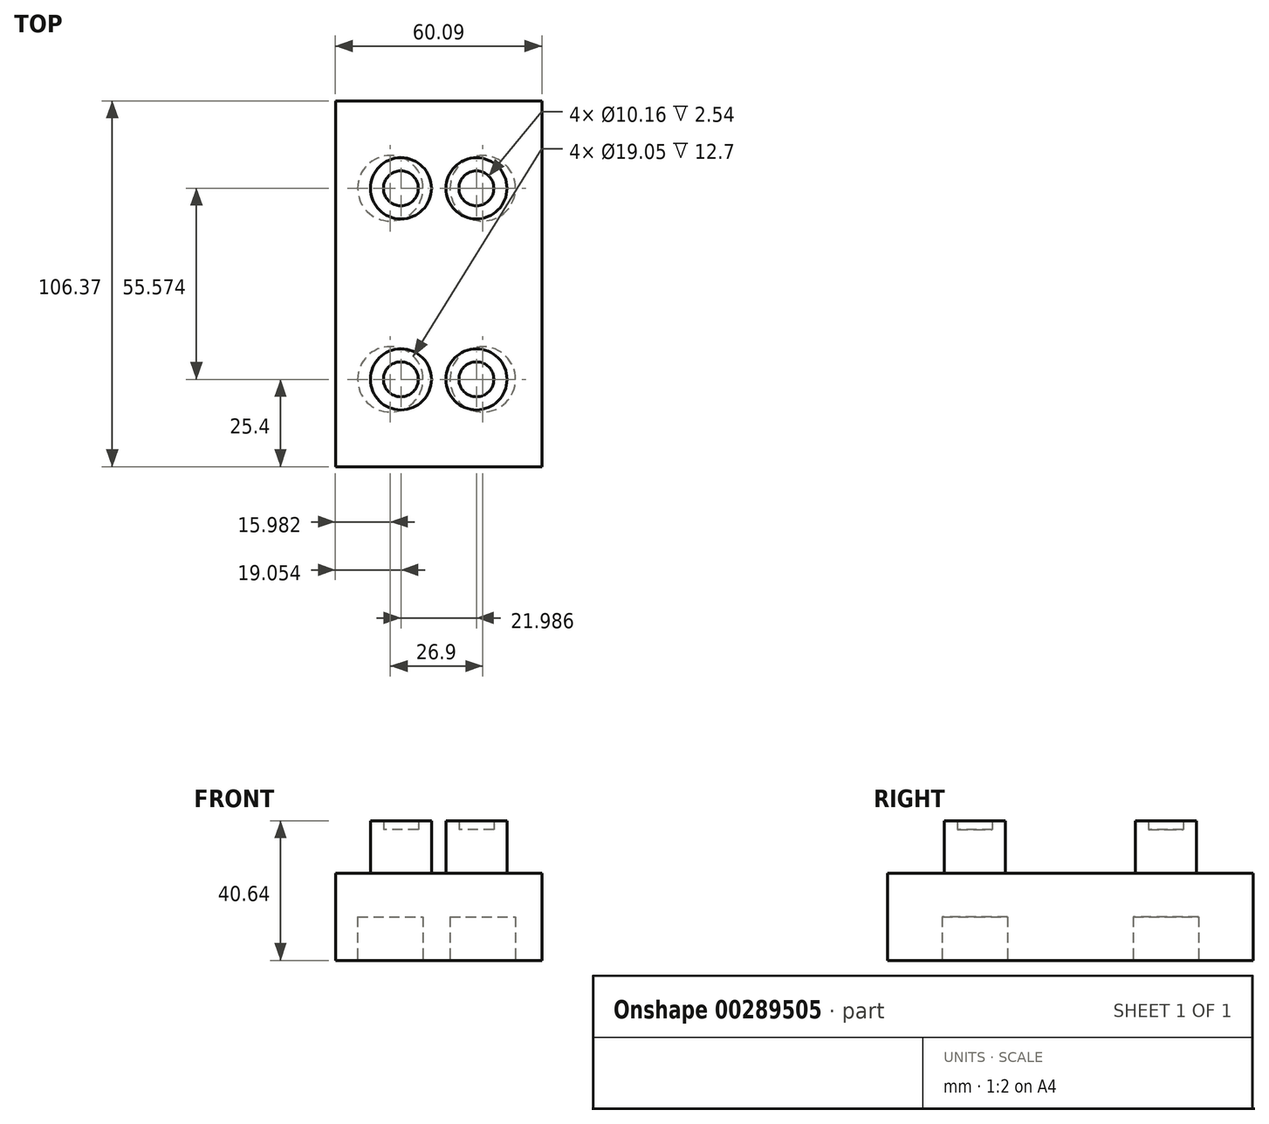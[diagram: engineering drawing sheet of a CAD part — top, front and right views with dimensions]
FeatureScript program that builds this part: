
annotation { "Feature Type Name" : "Feature", "Feature Type Description" : "" }
export const myFeature = defineFeature(function(context is Context, id is Id, definition is map)
    precondition{}
    {
        {
            var Q0;
            Q0=qCreatedBy(makeId("Top.planeOp"),FACE);
            var sketch = newSketch(context, id + "F0", { "sketchPlane" : qUnion([Q0])});
            skLineSegment(sketch, "E0.bottom", {"start": v(-60.09, -63.54) * mm, "end": v(0, -63.54) * mm});
            skLineSegment(sketch, "E0.top", {"start": v(-60.09, 42.83) * mm, "end": v(0, 42.83) * mm});
            skLineSegment(sketch, "E0.left", {"start": v(-60.09, -63.54) * mm, "end": v(-60.09, 42.83) * mm});
            skLineSegment(sketch, "E0.right", {"start": v(0, -63.54) * mm, "end": v(0, 42.83) * mm});
            skSolve(sketch);
        }
        {
            var Q0;
            Q0=makeQuery(id+"F0.imprint","IMPRINT",FACE,{"disambiguationData":[TD([[makeQuery(id+"F0.imprint","IMPRINT",EDGE,{"derivedFrom":sQuery(id+"F0.wireOp",EDGE,"E0.bottom")}),1.0]])]});
            extrude(context, id + "F1", {"entities" : qUnion([Q0]), "depth" : 25.4 * mm});
        }
        {
            var Q0;
            Q0=makeQuery(id+"F1.opExtrude","CAP_FACE",FACE,{"disambiguationData":[OSD([sQuery(id+"F0.wireOp",EDGE,"E0.bottom"),sQuery(id+"F0.wireOp",EDGE,"E0.top"),sQuery(id+"F0.wireOp",EDGE,"E0.left"),sQuery(id+"F0.wireOp",EDGE,"E0.right")])],"isStart":false});
            var sketch = newSketch(context, id + "F2", { "sketchPlane" : qUnion([Q0])});
            skLineSegment(sketch, "E1", {"start": v(-19.05, -63.54) * mm, "end": v(-19.05, -38.14) * mm});
            skLineSegment(sketch, "E2", {"start": v(-19.05, 42.83) * mm, "end": v(-19.05, 17.43) * mm});
            skLineSegment(sketch, "E3", {"start": v(0, 15.67) * mm, "end": v(-19.05, 15.67) * mm});
            skLineSegment(sketch, "E4", {"start": v(-60.09, 17.43) * mm, "end": v(-41.04, 17.43) * mm});
            skLineSegment(sketch, "E5", {"start": v(-41.04, 17.43) * mm, "end": v(-41.04, 42.83) * mm});
            skLineSegment(sketch, "E6", {"start": v(0, -38.14) * mm, "end": v(-19.05, -38.14) * mm});
            skLineSegment(sketch, "E7", {"start": v(-60.09, -38.14) * mm, "end": v(-41.04, -38.14) * mm});
            skLineSegment(sketch, "E8", {"start": v(-41.04, -38.14) * mm, "end": v(-41.04, -63.54) * mm});
            skCircle(sketch, "E9", {"center": v(-19.05, -38.14) * mm, "radius": 8.9 * mm});
            skCircle(sketch, "E10", {"center": v(-41.04, -38.14) * mm, "radius": 8.9 * mm});
            skCircle(sketch, "E11", {"center": v(-41.04, 17.43) * mm, "radius": 8.9 * mm});
            skCircle(sketch, "E12", {"center": v(-19.05, 17.43) * mm, "radius": 8.9 * mm});
            skSolve(sketch);
        }
        {
            var Q0;
            {var subQ0=sQuery(id+"F2.wireOp",EDGE,"E6");var subQ1=sQuery(id+"F2.wireOp",EDGE,"E1");var subQ2=makeQuery(id+"F2.imprint","INTERSECT",VERTEX,{"derivedFrom":[subQ1,subQ0]});Q0=makeQuery(id+"F2.imprint","IMPRINT",FACE,{"disambiguationData":[TD([[makeQuery(id+"F2.imprint","IMPRINT",EDGE,{"disambiguationData":[TD([[subQ2,1.0]])],"derivedFrom":subQ1}),1.0]])]});}
            var Q1;
            {var subQ0=sQuery(id+"F2.wireOp",EDGE,"E6");var subQ1=sQuery(id+"F2.wireOp",EDGE,"E1");var subQ2=makeQuery(id+"F2.imprint","INTERSECT",VERTEX,{"derivedFrom":[subQ1,subQ0]});Q1=makeQuery(id+"F2.imprint","IMPRINT",FACE,{"disambiguationData":[TD([[makeQuery(id+"F2.imprint","IMPRINT",EDGE,{"disambiguationData":[TD([[subQ2,1.0]])],"derivedFrom":subQ1}),-1.0]])]});}
            var Q2;
            {var subQ0=sQuery(id+"F2.wireOp",EDGE,"E8");var subQ1=sQuery(id+"F2.wireOp",EDGE,"E7");var subQ2=makeQuery(id+"F2.imprint","INTERSECT",VERTEX,{"derivedFrom":[subQ1,subQ0]});Q2=makeQuery(id+"F2.imprint","IMPRINT",FACE,{"disambiguationData":[TD([[makeQuery(id+"F2.imprint","IMPRINT",EDGE,{"disambiguationData":[TD([[subQ2,1.0]])],"derivedFrom":subQ1}),-1.0]])]});}
            var Q3;
            {var subQ0=sQuery(id+"F2.wireOp",EDGE,"E8");var subQ1=sQuery(id+"F2.wireOp",EDGE,"E7");var subQ2=makeQuery(id+"F2.imprint","INTERSECT",VERTEX,{"derivedFrom":[subQ1,subQ0]});Q3=makeQuery(id+"F2.imprint","IMPRINT",FACE,{"disambiguationData":[TD([[makeQuery(id+"F2.imprint","IMPRINT",EDGE,{"disambiguationData":[TD([[subQ2,1.0]])],"derivedFrom":subQ1}),1.0]])]});}
            var Q4;
            {var subQ0=sQuery(id+"F2.wireOp",EDGE,"E5");var subQ1=sQuery(id+"F2.wireOp",EDGE,"E4");var subQ2=makeQuery(id+"F2.imprint","INTERSECT",VERTEX,{"derivedFrom":[subQ1,subQ0]});Q4=makeQuery(id+"F2.imprint","IMPRINT",FACE,{"disambiguationData":[TD([[makeQuery(id+"F2.imprint","IMPRINT",EDGE,{"disambiguationData":[TD([[subQ2,1.0]])],"derivedFrom":subQ1}),1.0]])]});}
            var Q5;
            {var subQ0=sQuery(id+"F2.wireOp",EDGE,"E5");var subQ1=sQuery(id+"F2.wireOp",EDGE,"E4");var subQ2=makeQuery(id+"F2.imprint","INTERSECT",VERTEX,{"derivedFrom":[subQ1,subQ0]});Q5=makeQuery(id+"F2.imprint","IMPRINT",FACE,{"disambiguationData":[TD([[makeQuery(id+"F2.imprint","IMPRINT",EDGE,{"disambiguationData":[TD([[subQ2,1.0]])],"derivedFrom":subQ1}),-1.0]])]});}
            var Q6;
            {var subQ0=sQuery(id+"F2.wireOp",EDGE,"E12");var subQ1=makeQuery(id+"F2.imprint","INTERSECT",VERTEX,{"derivedFrom":[sQuery(id+"F2.wireOp",EDGE,"E2"),subQ0]});Q6=makeQuery(id+"F2.imprint","IMPRINT",FACE,{"disambiguationData":[TD([[makeQuery(id+"F2.imprint","IMPRINT",EDGE,{"disambiguationData":[TD([[subQ1,-1.0]])],"derivedFrom":subQ0}),1.0]])]});}
            extrude(context, id + "F3", {"entities" : qUnion([Q0, Q1, Q2, Q3, Q4, Q5, Q6]), "operationType" : NewBodyOperationType.ADD, "depth" : 12.7 * mm});
        }
        {
            var Q0;
            Q0=makeQuery(id+"F1.opExtrude","CAP_FACE",FACE,{"disambiguationData":[OSD([sQuery(id+"F0.wireOp",EDGE,"E0.bottom"),sQuery(id+"F0.wireOp",EDGE,"E0.top"),sQuery(id+"F0.wireOp",EDGE,"E0.left"),sQuery(id+"F0.wireOp",EDGE,"E0.right")])],"isStart":false});
            var sketch = newSketch(context, id + "F4", { "sketchPlane" : qUnion([Q0])});
            skCircle(sketch, "E13", {"center": v(-41.04, -38.14) * mm, "radius": 5.08 * mm});
            skCircle(sketch, "E14", {"center": v(-19.05, -38.14) * mm, "radius": 5.08 * mm});
            skCircle(sketch, "E15", {"center": v(-19.05, 17.43) * mm, "radius": 5.08 * mm});
            skCircle(sketch, "E16", {"center": v(-41.04, 17.43) * mm, "radius": 5.08 * mm});
            skSolve(sketch);
        }
        {
            var Q0;
            Q0=makeQuery(id+"F4.imprint","IMPRINT",FACE,{"disambiguationData":[TD([[makeQuery(id+"F4.imprint","IMPRINT",EDGE,{"derivedFrom":sQuery(id+"F4.wireOp",EDGE,"E13")}),-1.0]])]});
            var Q1;
            Q1=makeQuery(id+"F4.imprint","IMPRINT",FACE,{"disambiguationData":[TD([[makeQuery(id+"F4.imprint","IMPRINT",EDGE,{"derivedFrom":sQuery(id+"F4.wireOp",EDGE,"E14")}),-1.0]])]});
            var Q2;
            Q2=makeQuery(id+"F4.imprint","IMPRINT",FACE,{"disambiguationData":[TD([[makeQuery(id+"F4.imprint","IMPRINT",EDGE,{"derivedFrom":sQuery(id+"F4.wireOp",EDGE,"E16")}),-1.0]])]});
            var Q3;
            Q3=makeQuery(id+"F4.imprint","IMPRINT",FACE,{"disambiguationData":[TD([[makeQuery(id+"F4.imprint","IMPRINT",EDGE,{"derivedFrom":sQuery(id+"F4.wireOp",EDGE,"E15")}),-1.0]])]});
            extrude(context, id + "F5", {"entities" : qUnion([Q0, Q1, Q2, Q3]), "operationType" : NewBodyOperationType.ADD, "depth" : 15.24 * mm});
        }
        {
            var Q0;
            Q0=makeQuery(id+"F1.opExtrude","CAP_FACE",FACE,{"disambiguationData":[OSD([sQuery(id+"F0.wireOp",EDGE,"E0.bottom"),sQuery(id+"F0.wireOp",EDGE,"E0.top"),sQuery(id+"F0.wireOp",EDGE,"E0.left"),sQuery(id+"F0.wireOp",EDGE,"E0.right")])],"isStart":true});
            var sketch = newSketch(context, id + "F6", { "sketchPlane" : qUnion([Q0])});
            skLineSegment(sketch, "E17", {"start": v(-60.09, 38.14) * mm, "end": v(0, 38.14) * mm});
            skLineSegment(sketch, "E18", {"start": v(-60.09, -17.43) * mm, "end": v(0, -17.43) * mm});
            skLineSegment(sketch, "E19", {"start": v(-50.73, -17.43) * mm, "end": v(-50.73, -42.83) * mm});
            skLineSegment(sketch, "E20", {"start": v(-48.35, 63.54) * mm, "end": v(-48.35, 38.14) * mm});
            skCircle(sketch, "E21", {"center": v(-44.1, -17.43) * mm, "radius": 9.53 * mm});
            skCircle(sketch, "E22", {"center": v(-44.1, 38.14) * mm, "radius": 9.53 * mm});
            skCircle(sketch, "E23", {"center": v(-17.2, 38.14) * mm, "radius": 9.53 * mm});
            skCircle(sketch, "E24", {"center": v(-17.2, -17.43) * mm, "radius": 9.53 * mm});
            skSolve(sketch);
        }
        {
            var Q0;
            {var subQ0=sQuery(id+"F6.wireOp",EDGE,"E20");var subQ1=sQuery(id+"F6.wireOp",EDGE,"E17");var subQ2=makeQuery(id+"F6.imprint","INTERSECT",VERTEX,{"derivedFrom":[subQ1,subQ0]});Q0=makeQuery(id+"F6.imprint","IMPRINT",FACE,{"disambiguationData":[TD([[makeQuery(id+"F6.imprint","IMPRINT",EDGE,{"disambiguationData":[TD([[subQ2,1.0]])],"derivedFrom":subQ1}),1.0]])]});}
            var Q1;
            {var subQ0=sQuery(id+"F6.wireOp",EDGE,"E17");var subQ1=makeQuery(id+"F6.imprint","INTERSECT",VERTEX,{"derivedFrom":[subQ0,sQuery(id+"F6.wireOp",EDGE,"E20")]});Q1=makeQuery(id+"F6.imprint","IMPRINT",FACE,{"disambiguationData":[TD([[makeQuery(id+"F6.imprint","IMPRINT",EDGE,{"disambiguationData":[TD([[subQ1,1.0]])],"derivedFrom":subQ0}),-1.0]])]});}
            var Q2;
            {var subQ0=sQuery(id+"F6.wireOp",EDGE,"E20");var subQ1=sQuery(id+"F6.wireOp",EDGE,"E17");var subQ2=makeQuery(id+"F6.imprint","INTERSECT",VERTEX,{"derivedFrom":[subQ1,subQ0]});Q2=makeQuery(id+"F6.imprint","IMPRINT",FACE,{"disambiguationData":[TD([[makeQuery(id+"F6.imprint","IMPRINT",EDGE,{"disambiguationData":[TD([[subQ2,-1.0]])],"derivedFrom":subQ1}),1.0]])]});}
            var Q3;
            {var subQ0=sQuery(id+"F6.wireOp",EDGE,"E23");var subQ1=sQuery(id+"F6.wireOp",EDGE,"E17");var subQ2=makeQuery(id+"F6.imprint","INTERSECT",VERTEX,{"disambiguationData":[OD(0.0)],"derivedFrom":[subQ1,subQ0]});Q3=makeQuery(id+"F6.imprint","IMPRINT",FACE,{"disambiguationData":[TD([[makeQuery(id+"F6.imprint","IMPRINT",EDGE,{"disambiguationData":[TD([[subQ2,-1.0]])],"derivedFrom":subQ1}),-1.0]])]});}
            var Q4;
            {var subQ0=sQuery(id+"F6.wireOp",EDGE,"E23");var subQ1=sQuery(id+"F6.wireOp",EDGE,"E17");var subQ2=makeQuery(id+"F6.imprint","INTERSECT",VERTEX,{"disambiguationData":[OD(0.0)],"derivedFrom":[subQ1,subQ0]});Q4=makeQuery(id+"F6.imprint","IMPRINT",FACE,{"disambiguationData":[TD([[makeQuery(id+"F6.imprint","IMPRINT",EDGE,{"disambiguationData":[TD([[subQ2,-1.0]])],"derivedFrom":subQ1}),1.0]])]});}
            var Q5;
            {var subQ0=sQuery(id+"F6.wireOp",EDGE,"E24");var subQ1=sQuery(id+"F6.wireOp",EDGE,"E18");var subQ2=makeQuery(id+"F6.imprint","INTERSECT",VERTEX,{"disambiguationData":[OD(0.0)],"derivedFrom":[subQ1,subQ0]});Q5=makeQuery(id+"F6.imprint","IMPRINT",FACE,{"disambiguationData":[TD([[makeQuery(id+"F6.imprint","IMPRINT",EDGE,{"disambiguationData":[TD([[subQ2,-1.0]])],"derivedFrom":subQ1}),-1.0]])]});}
            var Q6;
            {var subQ0=sQuery(id+"F6.wireOp",EDGE,"E24");var subQ1=sQuery(id+"F6.wireOp",EDGE,"E18");var subQ2=makeQuery(id+"F6.imprint","INTERSECT",VERTEX,{"disambiguationData":[OD(0.0)],"derivedFrom":[subQ1,subQ0]});Q6=makeQuery(id+"F6.imprint","IMPRINT",FACE,{"disambiguationData":[TD([[makeQuery(id+"F6.imprint","IMPRINT",EDGE,{"disambiguationData":[TD([[subQ2,-1.0]])],"derivedFrom":subQ1}),1.0]])]});}
            var Q7;
            {var subQ0=sQuery(id+"F6.wireOp",EDGE,"E19");var subQ1=sQuery(id+"F6.wireOp",EDGE,"E18");var subQ2=makeQuery(id+"F6.imprint","INTERSECT",VERTEX,{"derivedFrom":[subQ1,subQ0]});Q7=makeQuery(id+"F6.imprint","IMPRINT",FACE,{"disambiguationData":[TD([[makeQuery(id+"F6.imprint","IMPRINT",EDGE,{"disambiguationData":[TD([[subQ2,-1.0]])],"derivedFrom":subQ1}),-1.0]])]});}
            var Q8;
            {var subQ0=sQuery(id+"F6.wireOp",EDGE,"E19");var subQ1=sQuery(id+"F6.wireOp",EDGE,"E18");var subQ2=makeQuery(id+"F6.imprint","INTERSECT",VERTEX,{"derivedFrom":[subQ1,subQ0]});Q8=makeQuery(id+"F6.imprint","IMPRINT",FACE,{"disambiguationData":[TD([[makeQuery(id+"F6.imprint","IMPRINT",EDGE,{"disambiguationData":[TD([[subQ2,1.0]])],"derivedFrom":subQ1}),-1.0]])]});}
            var Q9;
            {var subQ0=sQuery(id+"F6.wireOp",EDGE,"E18");var subQ1=makeQuery(id+"F6.imprint","INTERSECT",VERTEX,{"derivedFrom":[subQ0,sQuery(id+"F6.wireOp",EDGE,"E19")]});Q9=makeQuery(id+"F6.imprint","IMPRINT",FACE,{"disambiguationData":[TD([[makeQuery(id+"F6.imprint","IMPRINT",EDGE,{"disambiguationData":[TD([[subQ1,1.0]])],"derivedFrom":subQ0}),1.0]])]});}
            extrude(context, id + "F7", {"entities" : qUnion([Q0, Q1, Q2, Q3, Q4, Q5, Q6, Q7, Q8, Q9]), "operationType" : NewBodyOperationType.REMOVE, "oppositeDirection" : true, "depth" : 12.7 * mm});
        }
    });
